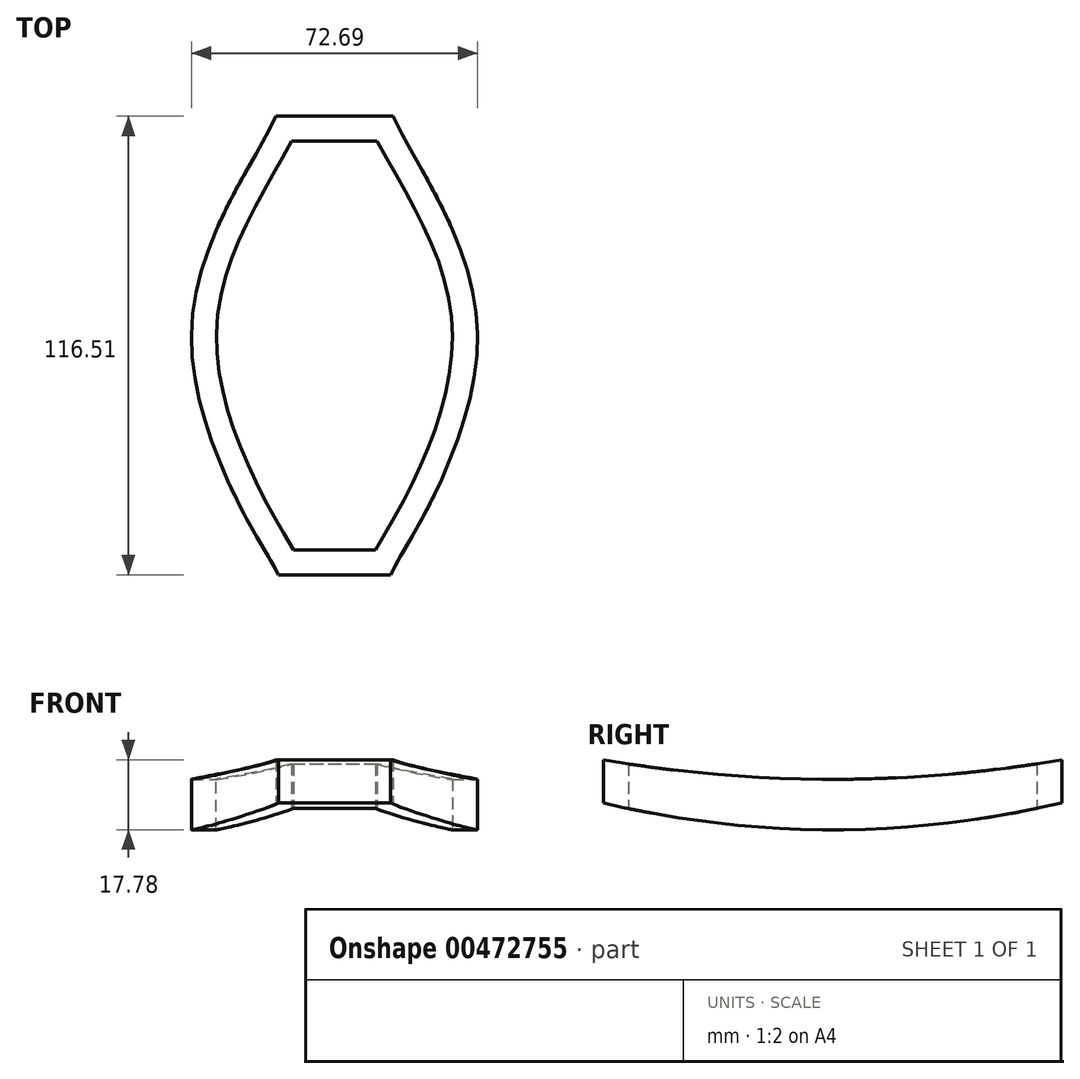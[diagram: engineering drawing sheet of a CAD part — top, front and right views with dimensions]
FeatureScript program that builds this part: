
annotation { "Feature Type Name" : "Feature", "Feature Type Description" : "" }
export const myFeature = defineFeature(function(context is Context, id is Id, definition is map)
    precondition{}
    {
        {
            var Q0;
            Q0=qCreatedBy(makeId("Top.planeOp"),FACE);
            var sketch = newSketch(context, id + "F0", { "sketchPlane" : qUnion([Q0])});
            skLineSegment(sketch, "E0", {"start": v(-14.25, -58.17) * mm, "end": v(0, -58.17) * mm});
            skLineSegment(sketch, "E1", {"start": v(-14.87, 58.34) * mm, "end": v(0, 58.34) * mm});
            skFitSpline(sketch, "E2", {"points": [v(-14.25, -58.17) * mm, v(-23.54, -41.57) * mm, v(-36.31, 0) * mm, v(-26.7, 36.44) * mm, v(-14.87, 58.34) * mm], "startDerivative": vector(-37.4, 74.17) * mm, "endDerivative": vector(41.95, 91.18) * mm});
            skLineSegment(sketch, "E3", {"start": v(0, -51.82) * mm, "end": v(0, -58.17) * mm});
            skLineSegment(sketch, "E4", {"start": v(0, 52) * mm, "end": v(0, 58.34) * mm});
            skLineSegment(sketch, "E5.0", {"start": v(-10.91, 52) * mm, "end": v(0, 52) * mm});
            skFitSpline(sketch, "E5.1", {"points": [v(-8.58, -55.3) * mm, v(-9.44, -53.6) * mm, v(-11.26, -50.35) * mm, v(-13.7, -46.25) * mm, v(-15.75, -42.64) * mm, v(-17.1, -40.19) * mm, v(-18.2, -38.07) * mm, v(-19.33, -35.83) * mm, v(-20.77, -32.84) * mm, v(-22.48, -29) * mm, v(-24.69, -23.58) * mm, v(-26.67, -17.85) * mm, v(-28.23, -12.03) * mm, v(-29, -8.4) * mm, v(-29.45, -5.53) * mm, v(-29.72, -3.4) * mm, v(-29.9, -1.3) * mm, v(-30, 0.74) * mm, v(-30, 2.76) * mm, v(-29.9, 5.45) * mm, v(-29.56, 8.76) * mm, v(-28.88, 12.68) * mm, v(-27.62, 17.81) * mm, v(-25.93, 22.78) * mm, v(-23.94, 27.54) * mm, v(-22.34, 31) * mm, v(-20.67, 34.33) * mm, v(-18.96, 37.52) * mm, v(-17.24, 40.61) * mm, v(-14.94, 44.65) * mm, v(-12.13, 49.6) * mm, v(-10.06, 53.62) * mm, v(-9.1, 55.69) * mm]});
            skLineSegment(sketch, "E5.2", {"start": v(-10.45, -51.82) * mm, "end": v(0, -51.82) * mm});
            skSolve(sketch);
        }
        {
            var Q0;
            {var subQ4=sQuery(id+"F0.wireOp",EDGE,"E0");Q0=makeQuery(id+"F0.imprint","IMPRINT",FACE,{"disambiguationData":[TD([[makeQuery(id+"F0.imprint","IMPRINT",EDGE,{"derivedFrom":subQ4}),1.0]])]});}
            extrude(context, id + "F1", {"entities" : qUnion([Q0]), "depth" : 17.78 * mm});
        }
        {
            var Q0;
            Q0=makeQuery(id+"F1.opExtrude","SWEPT_BODY",BODY,{"disambiguationData":[OSD([sQuery(id+"F0.wireOp",EDGE,"E0"),sQuery(id+"F0.wireOp",EDGE,"E1"),sQuery(id+"F0.wireOp",EDGE,"E2"),sQuery(id+"F0.wireOp",EDGE,"E3"),sQuery(id+"F0.wireOp",EDGE,"E4"),sQuery(id+"F0.wireOp",EDGE,"E5.0"),sQuery(id+"F0.wireOp",EDGE,"E5.1"),sQuery(id+"F0.wireOp",EDGE,"E5.2")])]});
            var Q1;
            Q1=qCreatedBy(makeId("Right.planeOp"),FACE);
            mirror(context, id + "F2", {"operationType" : NewBodyOperationType.ADD, "entities" : qUnion([Q0]), "mirrorPlane" : qUnion([Q1])});
        }
        {
            var Q0;
            Q0=qCreatedBy(makeId("Right.planeOp"),FACE);
            var sketch = newSketch(context, id + "F3", { "sketchPlane" : qUnion([Q0])});
            skArc(sketch, "E6", {"start": v(-140.52, 42.75) * mm, "mid": v(0, 0) * mm, "end": v(140.52, 42.75) * mm});
            skArc(sketch, "E7", {"start": v(-140.52, 42.75) * mm, "mid": v(0, 12.8) * mm, "end": v(140.52, 42.75) * mm});
            skSolve(sketch);
        }
        {
            var Q0;
            Q0=makeQuery(id+"F3.imprint","IMPRINT",FACE,{"disambiguationData":[TD([[makeQuery(id+"F3.imprint","IMPRINT",EDGE,{"derivedFrom":sQuery(id+"F3.wireOp",EDGE,"E6")}),1.0]])]});
            extrude(context, id + "F4", {"entities" : qUnion([Q0]), "operationType" : NewBodyOperationType.INTERSECT, "oppositeDirection" : true, "depth" : 50.8 * mm, "hasSecondDirection" : true, "secondDirectionOppositeDirection" : false, "secondDirectionDepth" : 50.8 * mm});
        }
    });
